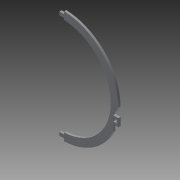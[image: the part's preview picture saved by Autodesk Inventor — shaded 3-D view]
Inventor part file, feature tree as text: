
AUTODESK INVENTOR PART (.ipt)
format: ipt  version: 2013 (Build 170138000, 138)  size: 125,440 bytes
history: native  units: in
note: dims shown in document units (in); Inventor stores cm internally (conversion verified against a paired STEP export)
features: extrude x2, sketch x1
ambient origin geometry x8: Origin, YZ Plane, XZ Plane, XY Plane, X Axis, Y Axis, Z Axis, Center Point
feature tree (3):
  extrude  "Extrusion2"  Depth=13.3in
  extrude  "Extrusion4"  Depth=0.25in
  sketch  "Sketch2"  dims[d0=11.5in d1=13.3in d7=0.25in d8=0.25in d9=0.2in d10=0.55in d11=0.4in d12=0.2in d13=0.55in d14=0.4in d15=2.0in d16=0.2054in d19=0.25in d20=0.0in d21=0.298in d22=0.2in d23=0.4in d24=0.375in d27=0.6in d28=0.923in d29=0.6in d30=1.0in d31=0.0in]
